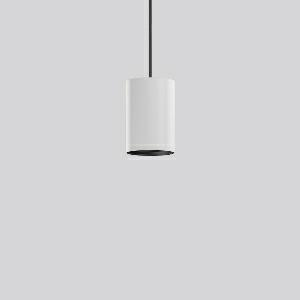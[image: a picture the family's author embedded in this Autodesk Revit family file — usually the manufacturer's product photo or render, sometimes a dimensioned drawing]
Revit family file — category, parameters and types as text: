
# Revit family: deecos_p_maxi_911547_002_9e04
name_source: partatom
category: Lighting Fixtures
units: mm (PartAtom-declared; Revit-internal decimal feet)

## family parameters
Cut with Voids When Loaded = No
Host = Face
Light Source = No
Part Type = Normal
Room Calculation Point = No
Round Connector Dimension = Use Diameter
Shared = No

## types (1)
- DEECOS P maxi (1 x LED Modul 932 fresh meat, 1800 lm, 3200)
    Apparent Load = 33 VA
    Approval mark = CE
    CIE Flux Codes = 97 100 100 100 100
    Color Rendering = 90
    Color Temperature = 3200
    Default Elevation = 1800 mm  [stored 5.90551 ft]
    Description = Series: DEECOS P maxi
Cylindrical pendant luminaire. Housing: die-cast aluminium, powder-coated. Canopy made of powder-coated sheet steel with magnetic attachment. Optical assembly with lens made of plastic (polycarbonate) for the best homogeneous light distribution - can be changed without tools. Including special LED for illuminating meat products / Meat fresh - reddish white. Transparent suspension cable 2 m, can be shortened. High quality converter without flickering and stroboscopic effect. The following accessories can be mounted without use of tools: interchangeable lenses, honeycomb louvre, clear and frosted diffusers, white interchangeable plastic ring. Decorative recessed suspension set available as accessory. 
Colour: traffic white, matt (RAL 9016)
Diameter: 123 mm
Height: 181 mm
Suspension length: 2000 mm
Lamp: LED
Socket: without socket
Colour temperature: fresh meat
Colour rendering index (CRI): 92
System power: 33 W
Rated luminous flux: 1800 lm
Luminous efficiency: 55 lm/W
Control gear: Regulated power supply
Protection class: I
Type of protection: IP 20
    Height = 181 mm
    Lamp = 1 x LED Modul 932 fresh meat
    Lamp Light Flux = 1800 lm
    Lamp count = 1
    Length = 123 mm
    Lifetime = 50000 h
    Luminous efficacy = 55 lm/W
    Manufacturer = RZB
    ModVariant = No
    Model = 911547.002
    Mounting Place = Ceiling
    Mounting Type = Pendant
    Number of Poles = 1
    OnlyDefault = Yes
    Power Factor = 1
    Product Name = DEECOS P maxi
    Product group = Pendant luminaires
    ProductGroupID = 902
    Protection Class = Protection class I
    Protection Degree = IP 20
    RLX_Detail_Level = 1
    RLX_Emergency_Light_Flux = 0 lm
    RLX_Emergency_Type = 0
    RLX_Emergency_Type_DB = No
    RlxData = <blob elided: 35949 chars, md5=ed6ed3c9>
    Socket = socket
    Standby Power = 0 W
    System Light Flux = 1800 lm
    System Power = 33 W
    Type Comments = Product without accessories
    Type Image = 911480.002.jpg
    URL = http://relux.com
    VarID = ---
    Voltage = 230 V
    Voltage Range = 220-240 V
    Weight = 0.00 kg
    Width = 0 mm  [stored 0 ft]

note: [stored X ft] marks values corroborated as IEEE doubles in the binary element streams (Revit-internal decimal feet)

## geometry (parser evidence)
native form markers: Blend x4, Sweep x11
no freeform markers — native parametric forms only
